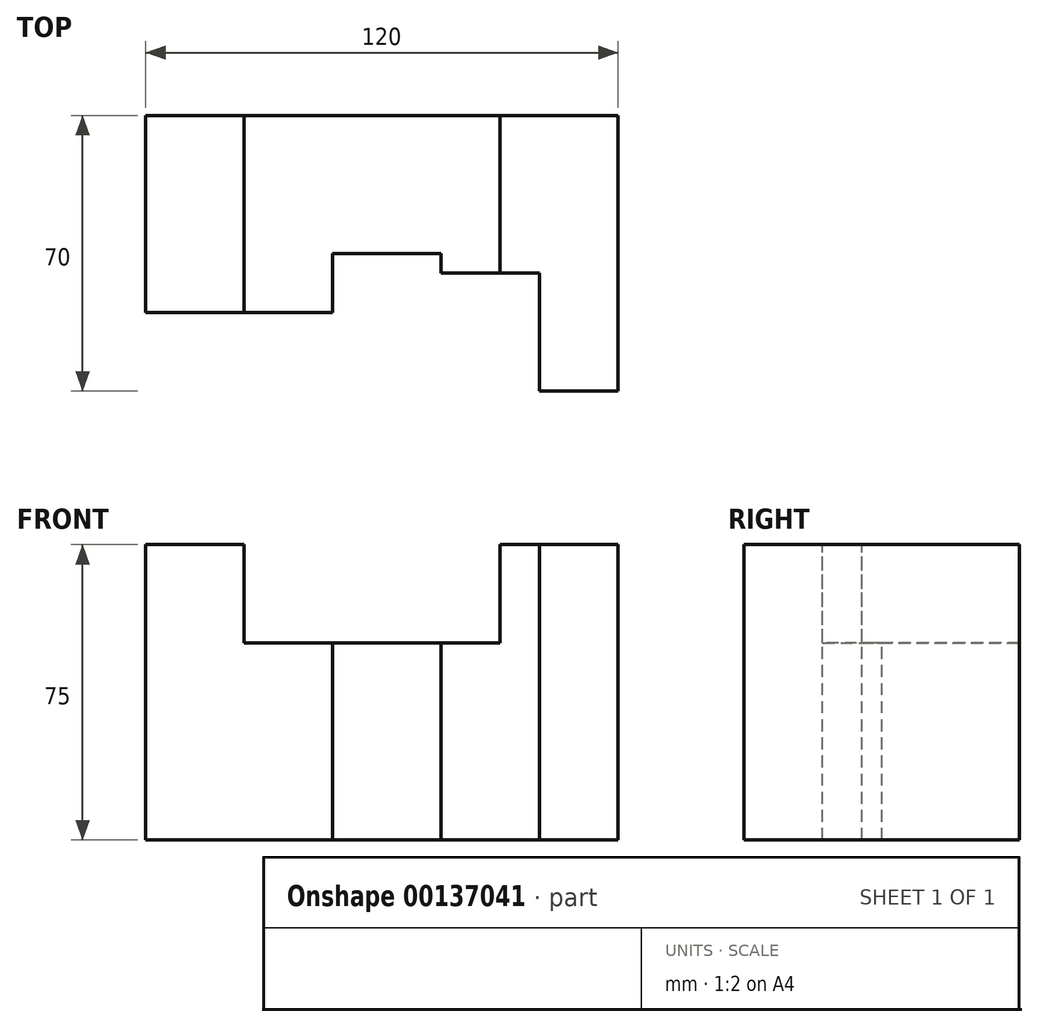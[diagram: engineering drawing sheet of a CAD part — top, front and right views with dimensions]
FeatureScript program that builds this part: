
annotation { "Feature Type Name" : "Feature", "Feature Type Description" : "" }
export const myFeature = defineFeature(function(context is Context, id is Id, definition is map)
    precondition{}
    {
        {
            var Q0;
            Q0=qCreatedBy(makeId("Top.planeOp"),FACE);
            var sketch = newSketch(context, id + "F0", { "sketchPlane" : qUnion([Q0])});
            skLineSegment(sketch, "E0.bottom", {"start": v(0, 0) * mm, "end": v(110, 0) * mm});
            skLineSegment(sketch, "E0.top", {"start": v(0, 70) * mm, "end": v(110, 70) * mm});
            skLineSegment(sketch, "E0.left", {"start": v(0, 0) * mm, "end": v(0, 70) * mm});
            skLineSegment(sketch, "E0.right", {"start": v(110, 0) * mm, "end": v(110, 70) * mm});
            skSolve(sketch);
        }
        {
            var Q0;
            Q0 = qSketchRegion(id + "F0", true);
            extrude(context, id + "F1", {"entities" : qUnion([Q0]), "depth" : 75 * mm});
        }
        {
            var Q0;
            Q0=makeQuery(id+"F1.opExtrude","CAP_FACE",FACE,{"disambiguationData":[OSD([sQuery(id+"F0.wireOp",EDGE,"E0.bottom"),sQuery(id+"F0.wireOp",EDGE,"E0.top"),sQuery(id+"F0.wireOp",EDGE,"E0.left"),sQuery(id+"F0.wireOp",EDGE,"E0.right")])],"isStart":false});
            var sketch = newSketch(context, id + "F2", { "sketchPlane" : qUnion([Q0])});
            skLineSegment(sketch, "E1", {"start": v(90, 0) * mm, "end": v(90, 30) * mm});
            skLineSegment(sketch, "E2", {"start": v(90, 30) * mm, "end": v(75, 30) * mm});
            skLineSegment(sketch, "E3", {"start": v(75, 30) * mm, "end": v(75, 35) * mm});
            skLineSegment(sketch, "E4", {"start": v(75, 35) * mm, "end": v(47.5, 35) * mm});
            skLineSegment(sketch, "E5", {"start": v(0, 0) * mm, "end": v(90, 0) * mm});
            skLineSegment(sketch, "E6", {"start": v(47.5, 35) * mm, "end": v(47.5, 20) * mm});
            skLineSegment(sketch, "E7", {"start": v(47.5, 20) * mm, "end": v(0, 20) * mm});
            skLineSegment(sketch, "E8", {"start": v(0, 20) * mm, "end": v(0, 0) * mm});
            skSolve(sketch);
        }
        {
            var Q0;
            Q0 = qSketchRegion(id + "F2", true);
            extrude(context, id + "F3", {"entities" : qUnion([Q0]), "operationType" : NewBodyOperationType.REMOVE, "endBound" : BoundingType.THROUGH_ALL, "oppositeDirection" : true, "depth" : 25 * mm});
        }
        {
            var Q0;
            Q0=makeQuery(id+"F1.opExtrude","CAP_FACE",FACE,{"disambiguationData":[OSD([sQuery(id+"F0.wireOp",EDGE,"E0.bottom"),sQuery(id+"F0.wireOp",EDGE,"E0.top"),sQuery(id+"F0.wireOp",EDGE,"E0.left"),sQuery(id+"F0.wireOp",EDGE,"E0.right")])],"isStart":false});
            var sketch = newSketch(context, id + "F4", { "sketchPlane" : qUnion([Q0])});
            skLineSegment(sketch, "E9.bottom", {"start": v(25, 70) * mm, "end": v(90, 70) * mm});
            skLineSegment(sketch, "E9.top", {"start": v(25, 20) * mm, "end": v(90, 20) * mm});
            skLineSegment(sketch, "E9.left", {"start": v(25, 70) * mm, "end": v(25, 20) * mm});
            skLineSegment(sketch, "E9.right", {"start": v(90, 70) * mm, "end": v(90, 20) * mm});
            skSolve(sketch);
        }
        {
            var Q0;
            Q0 = qSketchRegion(id + "F4", true);
            extrude(context, id + "F5", {"entities" : qUnion([Q0]), "operationType" : NewBodyOperationType.REMOVE, "oppositeDirection" : true, "depth" : 25 * mm});
        }
        {
            var Q0;
            {var subQ0=sQuery(id+"F0.wireOp",EDGE,"E0.right");var subQ1=sQuery(id+"F0.wireOp",EDGE,"E0.top");var subQ2=sQuery(id+"F0.wireOp",EDGE,"E0.bottom");Q0=makeQuery(id+"F5.boolean.opBoolean","SPLIT",FACE,{"disambiguationData":[TD([makeQuery(id+"F1.opExtrude","SWEPT_FACE",FACE,{"disambiguationData":[OSD([subQ2])]})])],"derivedFrom":makeQuery(id+"F1.opExtrude","CAP_FACE",FACE,{"disambiguationData":[OSD([subQ2,subQ1,sQuery(id+"F0.wireOp",EDGE,"E0.left"),subQ0])],"isStart":false})});}
            var sketch = newSketch(context, id + "F6", { "sketchPlane" : qUnion([Q0])});
            skLineSegment(sketch, "E10.bottom", {"start": v(90, 0) * mm, "end": v(100, 0) * mm});
            skLineSegment(sketch, "E10.top", {"start": v(90, 30) * mm, "end": v(100, 30) * mm});
            skLineSegment(sketch, "E10.left", {"start": v(90, 0) * mm, "end": v(90, 30) * mm});
            skLineSegment(sketch, "E10.right", {"start": v(100, 0) * mm, "end": v(100, 30) * mm});
            skSolve(sketch);
        }
        {
            var Q0;
            Q0 = qSketchRegion(id + "F6", true);
            extrude(context, id + "F7", {"entities" : qUnion([Q0]), "operationType" : NewBodyOperationType.REMOVE, "endBound" : BoundingType.THROUGH_ALL, "oppositeDirection" : true, "depth" : 25 * mm});
        }
        {
            var Q0;
            Q0=makeQuery(id+"F1.opExtrude","SWEPT_FACE",FACE,{"disambiguationData":[OSD([sQuery(id+"F0.wireOp",EDGE,"E0.right")])]});
            var sketch = newSketch(context, id + "F8", { "sketchPlane" : qUnion([Q0])});
            skLineSegment(sketch, "E11.0", {"start": v(0, 75) * mm, "end": v(0, 0) * mm});
            skLineSegment(sketch, "E11.1", {"start": v(0, 0) * mm, "end": v(70, 0) * mm});
            skLineSegment(sketch, "E11.2", {"start": v(70, 75) * mm, "end": v(70, 0) * mm});
            skLineSegment(sketch, "E11.3", {"start": v(0, 75) * mm, "end": v(70, 75) * mm});
            skSolve(sketch);
        }
        {
            var Q0;
            Q0 = qSketchRegion(id + "F8", true);
            extrude(context, id + "F9", {"entities" : qUnion([Q0]), "operationType" : NewBodyOperationType.ADD, "depth" : 10 * mm});
        }
    });
